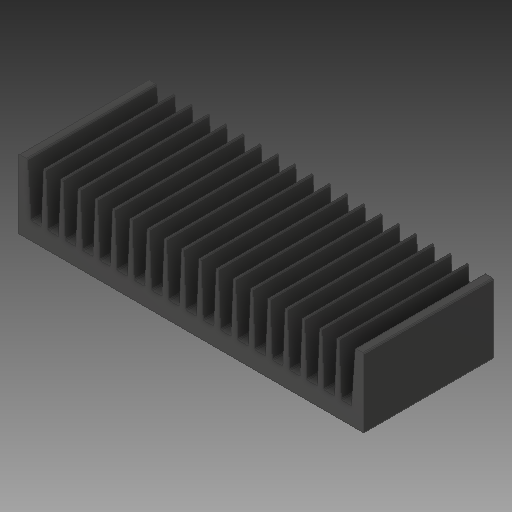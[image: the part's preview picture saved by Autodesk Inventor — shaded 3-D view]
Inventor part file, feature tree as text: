
AUTODESK INVENTOR PART (.ipt)
format: ipt  version: 2017 (Build 210142000, 142)  size: 244,224 bytes
history: native  units: in
note: dims shown in document units (in); Inventor stores cm internally (conversion verified against a paired STEP export)
features: fillet x1
ambient origin geometry x8: Origin, YZ Plane, XZ Plane, XY Plane, X Axis, Y Axis, Z Axis, Center Point
bodies: Solid1 (feature_tree)
feature tree (1):
  fillet  "Fillet1"  [1 undecoded]
note: 1 required parameter value undecoded (feature->parameter linkage not recoverable at this tier; creation-order binding heuristic only, values carry confidence <= 0.55)
